# Revit family: QF_BOURGEAT_chariot_cafeteria_12plateaux_modele_bas_couleur
name_source: partatom
category: Equipement spécialisé
revit_build: Autodesk Revit 2015 (Build: 20140606_1530(x64)
units: mm (PartAtom-declared; Revit-internal decimal feet)

## types (4) — shared parameters
Charge max = 60.00 kg
Fabricant = BOURGEAT
Hauteur hors tout = 994 mm
Longueur hors tout = 923 mm  [stored 3.02822 ft]
Profondeur hors tout = 618 mm  [stored 2.02756 ft]
Spécification du Fabricant = CHARIOT CAFETERIA
URL catalogue = http://www.bourgeat.fr

## per-type parameters (varying)
| type | Modèle | Poids net à vide | panneaux_bleus | panneaux_rouges | panneaux_verts |
| chariot_modele_bas_glissieres_beiges_sans_panneaux | 782426 | 17.00 kg | Non | Non | Non |
| chariot_modele_bas_glissieres_beiges_avec_panneaux_bleus | 782526 | 23.50 kg | Oui | Non | Non |
| chariot_modele_bas_glissieres_beiges_avec_panneaux_rouges | 782726 | 23.50 kg | Non | Oui | Non |
| chariot_modele_bas_glissieres_beiges_avec_panneaux_verts | 782626 | 23.50 kg | Non | Non | Oui |

note: [stored X ft] marks values corroborated as IEEE doubles in the binary element streams (Revit-internal decimal feet)
